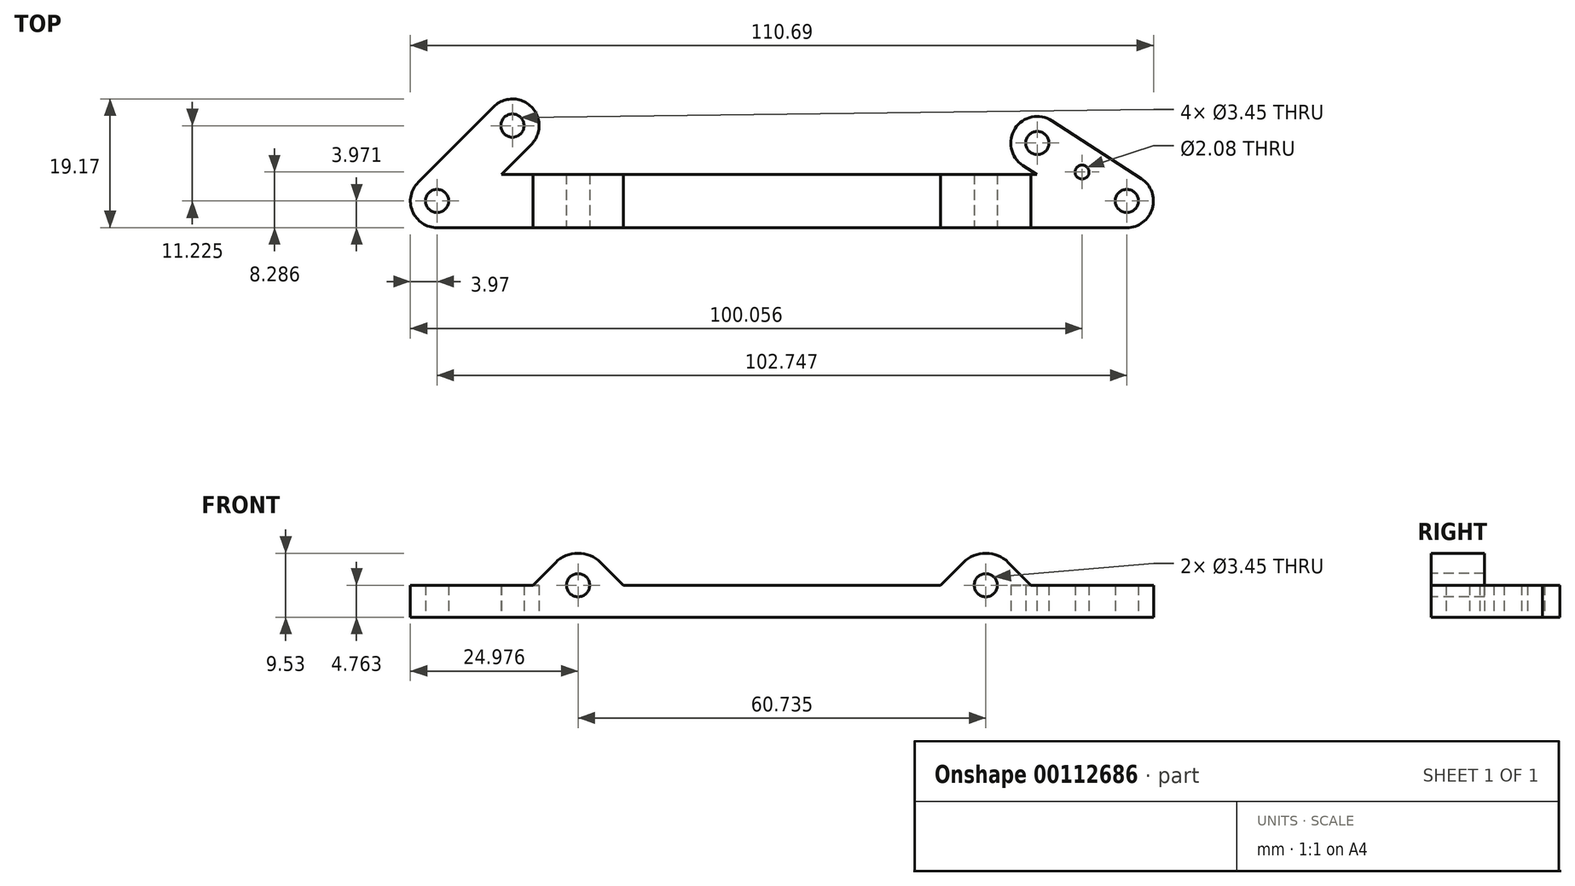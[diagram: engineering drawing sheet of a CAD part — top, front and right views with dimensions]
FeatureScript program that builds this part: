
annotation { "Feature Type Name" : "Feature", "Feature Type Description" : "" }
export const myFeature = defineFeature(function(context is Context, id is Id, definition is map)
    precondition{}
    {
        {
            var Q0;
            Q0=qCreatedBy(makeId("Top.planeOp"),FACE);
            var sketch = newSketch(context, id + "F0", { "sketchPlane" : qUnion([Q0])});
            skLineSegment(sketch, "E0", {"start": v(0, 0) * mm, "end": v(-79.74, 0) * mm});
            skLineSegment(sketch, "E1", {"start": v(0, 0) * mm, "end": v(-2.05, 1.33) * mm});
            skLineSegment(sketch, "E2", {"start": v(-79.74, 0) * mm, "end": v(-75.29, 4.45) * mm});
            skLineSegment(sketch, "E3", {"start": v(-39.87, 0) * mm, "end": v(-39.87, -7.94) * mm, "construction": true});
            skLineSegment(sketch, "E4", {"start": v(-89.32, -7.94) * mm, "end": v(13.43, -7.94) * mm});
            skLineSegment(sketch, "E5", {"start": v(-75.29, 4.45) * mm, "end": v(-80.9, 10.06) * mm, "construction": true});
            skLineSegment(sketch, "E6", {"start": v(-2.05, 1.33) * mm, "end": v(2.26, 8) * mm, "construction": true});
            skArc(sketch, "E7", {"start": v(-92.13, -1.16) * mm, "mid": v(-92.99, -5.49) * mm, "end": v(-89.32, -7.94) * mm});
            skArc(sketch, "E8", {"start": v(13.43, -7.94) * mm, "mid": v(17.23, -5.1) * mm, "end": v(15.59, -0.64) * mm});
            skArc(sketch, "E9", {"start": v(-75.29, 4.45) * mm, "mid": v(-75.29, 10.06) * mm, "end": v(-80.9, 10.06) * mm});
            skArc(sketch, "E10", {"start": v(2.26, 8) * mm, "mid": v(-3.23, 6.82) * mm, "end": v(-2.05, 1.33) * mm});
            skLineSegment(sketch, "E11", {"start": v(-89.32, -3.97) * mm, "end": v(-78.1, 7.26) * mm, "construction": true});
            skLineSegment(sketch, "E12", {"start": v(-92.13, -1.16) * mm, "end": v(-80.9, 10.06) * mm});
            skLineSegment(sketch, "E13", {"start": v(2.26, 8) * mm, "end": v(15.59, -0.64) * mm});
            skLineSegment(sketch, "E14", {"start": v(0.1, 4.66) * mm, "end": v(13.43, -3.97) * mm, "construction": true});
            skCircle(sketch, "E15", {"center": v(-78.1, 7.26) * mm, "radius": 1.73 * mm});
            skCircle(sketch, "E16", {"center": v(-89.32, -3.97) * mm, "radius": 1.73 * mm});
            skCircle(sketch, "E17", {"center": v(0.1, 4.66) * mm, "radius": 1.73 * mm});
            skCircle(sketch, "E18", {"center": v(13.43, -3.97) * mm, "radius": 1.73 * mm});
            skLineSegment(sketch, "E19", {"start": v(-39.87, 0) * mm, "end": v(-39.87, 2.49) * mm, "construction": true});
            skLineSegment(sketch, "E20", {"start": v(-39.87, 2.49) * mm, "end": v(-11.8, 30.55) * mm, "construction": true});
            skLineSegment(sketch, "E21", {"start": v(-25.84, 16.52) * mm, "end": v(-39.87, 30.55) * mm, "construction": true});
            skLineSegment(sketch, "E22", {"start": v(-39.87, 2.49) * mm, "end": v(-39.87, 30.55) * mm, "construction": true});
            skLineSegment(sketch, "E23", {"start": v(-39.87, 30.55) * mm, "end": v(0.1, 4.66) * mm, "construction": true});
            skCircle(sketch, "E24", {"center": v(6.77, 0.35) * mm, "radius": 1.04 * mm});
            skSolve(sketch);
        }
        {
            var Q0;
            Q0 = qSketchRegion(id + "F0", true);
            extrude(context, id + "F1", {"entities" : qUnion([Q0]), "depth" : 4.76 * mm});
        }
        {
            var Q0;
            Q0=makeQuery(id+"F1.opExtrude","SWEPT_FACE",FACE,{"disambiguationData":[OSD([sQuery(id+"F0.wireOp",EDGE,"E4")])]});
            var sketch = newSketch(context, id + "F2", { "sketchPlane" : qUnion([Q0])});
            skLineSegment(sketch, "E25", {"start": v(-89.32, 2.38) * mm, "end": v(-68.31, 2.38) * mm});
            skLineSegment(sketch, "E26", {"start": v(-68.31, 2.38) * mm, "end": v(-68.31, 4.76) * mm});
            skLineSegment(sketch, "E27", {"start": v(-68.31, 2.38) * mm, "end": v(-7.58, 2.38) * mm});
            skLineSegment(sketch, "E28", {"start": v(-7.58, 2.38) * mm, "end": v(13.43, 2.38) * mm});
            skLineSegment(sketch, "E29", {"start": v(-7.58, 2.38) * mm, "end": v(-7.58, 4.76) * mm});
            skArc(sketch, "E30", {"start": v(-4.21, 8.13) * mm, "mid": v(-7.58, 9.53) * mm, "end": v(-10.95, 8.13) * mm});
            skLineSegment(sketch, "E31", {"start": v(-10.95, 8.13) * mm, "end": v(-14.31, 4.76) * mm});
            skLineSegment(sketch, "E32", {"start": v(-4.21, 8.13) * mm, "end": v(-0.84, 4.76) * mm});
            skLineSegment(sketch, "E33", {"start": v(-14.31, 4.76) * mm, "end": v(-0.84, 4.76) * mm});
            skLineSegment(sketch, "E34", {"start": v(-75.05, 4.76) * mm, "end": v(-61.58, 4.76) * mm});
            skLineSegment(sketch, "E35", {"start": v(-75.05, 4.76) * mm, "end": v(-71.68, 8.13) * mm});
            skLineSegment(sketch, "E36", {"start": v(-61.58, 4.76) * mm, "end": v(-64.95, 8.13) * mm});
            skArc(sketch, "E37", {"start": v(-64.95, 8.13) * mm, "mid": v(-68.31, 9.52) * mm, "end": v(-71.68, 8.13) * mm});
            skSolve(sketch);
        }
        {
            var Q0;
            Q0 = qSketchRegion(id + "F2", true);
            var Q1;
            Q1=makeQuery(id+"F1.opExtrude","SWEPT_FACE",FACE,{"disambiguationData":[OSD([sQuery(id+"F0.wireOp",EDGE,"E0")])]});
            extrude(context, id + "F3", {"entities" : qUnion([Q0]), "operationType" : NewBodyOperationType.ADD, "endBound" : BoundingType.UP_TO_SURFACE, "oppositeDirection" : true, "endBoundEntityFace" : qUnion([Q1]), "depth" : 25.4 * mm});
        }
        {
            var Q0;
            Q0=makeQuery(id+"F3.boolean.opBoolean","MERGE",FACE,{"derivedFrom":[makeQuery(id+"F1.opExtrude","SWEPT_FACE",FACE,{"disambiguationData":[OSD([sQuery(id+"F0.wireOp",EDGE,"E4")])]}),makeQuery(id+"F3.opExtrude","CAP_FACE",FACE,{"disambiguationData":[OSD([sQuery(id+"F2.wireOp",EDGE,"E30"),sQuery(id+"F2.wireOp",EDGE,"E31"),sQuery(id+"F2.wireOp",EDGE,"E32"),sQuery(id+"F2.wireOp",EDGE,"E33")])],"isStart":true}),makeQuery(id+"F3.opExtrude","CAP_FACE",FACE,{"disambiguationData":[OSD([sQuery(id+"F2.wireOp",EDGE,"E34"),sQuery(id+"F2.wireOp",EDGE,"E35"),sQuery(id+"F2.wireOp",EDGE,"E36"),sQuery(id+"F2.wireOp",EDGE,"E37")])],"isStart":true})]});
            var sketch = newSketch(context, id + "F4", { "sketchPlane" : qUnion([Q0])});
            skCircle(sketch, "E38", {"center": v(-68.31, 4.76) * mm, "radius": 1.73 * mm});
            skCircle(sketch, "E39", {"center": v(-7.58, 4.76) * mm, "radius": 1.73 * mm});
            skSolve(sketch);
        }
        {
            var Q0;
            Q0 = qSketchRegion(id + "F4", true);
            var Q1;
            {var subQ0=sQuery(id+"F0.wireOp",EDGE,"E0");Q1=makeQuery(id+"F3.boolean.opBoolean","MERGE",FACE,{"derivedFrom":[makeQuery(id+"F1.opExtrude","SWEPT_FACE",FACE,{"disambiguationData":[OSD([subQ0])]}),makeQuery(id+"F3.opExtrude","CAP_FACE",FACE,{"disambiguationData":[OSD([subQ0]),ownerDisambiguation([makeQuery(id+"F3.opExtrude","SWEPT_BODY",BODY,{"disambiguationData":[OSD([sQuery(id+"F2.wireOp",EDGE,"E30"),sQuery(id+"F2.wireOp",EDGE,"E31"),sQuery(id+"F2.wireOp",EDGE,"E32"),sQuery(id+"F2.wireOp",EDGE,"E33")])]})])],"isStart":false}),makeQuery(id+"F3.opExtrude","CAP_FACE",FACE,{"disambiguationData":[OSD([subQ0]),ownerDisambiguation([makeQuery(id+"F3.opExtrude","SWEPT_BODY",BODY,{"disambiguationData":[OSD([sQuery(id+"F2.wireOp",EDGE,"E34"),sQuery(id+"F2.wireOp",EDGE,"E35"),sQuery(id+"F2.wireOp",EDGE,"E36"),sQuery(id+"F2.wireOp",EDGE,"E37")])]})])],"isStart":false})]});}
            extrude(context, id + "F5", {"entities" : qUnion([Q0]), "operationType" : NewBodyOperationType.REMOVE, "endBound" : BoundingType.UP_TO_SURFACE, "oppositeDirection" : true, "endBoundEntityFace" : qUnion([Q1]), "depth" : 25.4 * mm});
        }
    });
